# Revit family: Haworth_Openest_ChickPouf_Large
name_source: partatom
category: Furniture
revit_build: Autodesk Revit 2018 (Build: 20170223_1515(x64)
units: mm (PartAtom-declared; Revit-internal decimal feet)

## family parameters
Always vertical = Yes
Cut with Voids When Loaded = No
OmniClass Number = 23.40.20.00
OmniClass Title = General Furniture and Specialties
Room Calculation Point = No
Shared = No
Work Plane-Based = No

## types (3) — shared parameters
Assembly Code = E2020200
Description = Chick Pouf
Manufacturer = Haworth
Model = Openest Chick Pouf
Revision No. = 1
Round Pouf w/ Casters = No
Size = 24d 52w, 37d 37w, 65dia
Sustainability Info = https://www.haworth.com
URL = http://www.haworth.com
URL - Product = https://www.haworth.com
Warranty = http://www.haworth.com

## per-type parameters (varying)
| type | Caster Finish | Glide Finish | Rectangular Pouf  w/ Glides |
| Square Pouf w/ Glides | Haworth _ Polymer _ Black | Haworth _ Polymer _ Black | No |
| Round Pouf w/ Glides | Haworth _ Polymer _ Undecided | Haworth _ Polymer _ Undecided | No |
| Rectangular Pouf w/ Glides | Haworth _ Polymer _ Black | Haworth _ Polymer _ Black | Yes |

type visibility flags (boolean, named after types; folded from table):
- Square Pouf w/ Glides: Yes: Square Pouf w/ Glides
- Round Pouf w/ Glides: Yes: Round Pouf w/ Glides
- Rectangular Pouf w/ Glides: Yes: (none)

## geometry (parser evidence)
native form markers: Sweep x4
no freeform markers — native parametric forms only
